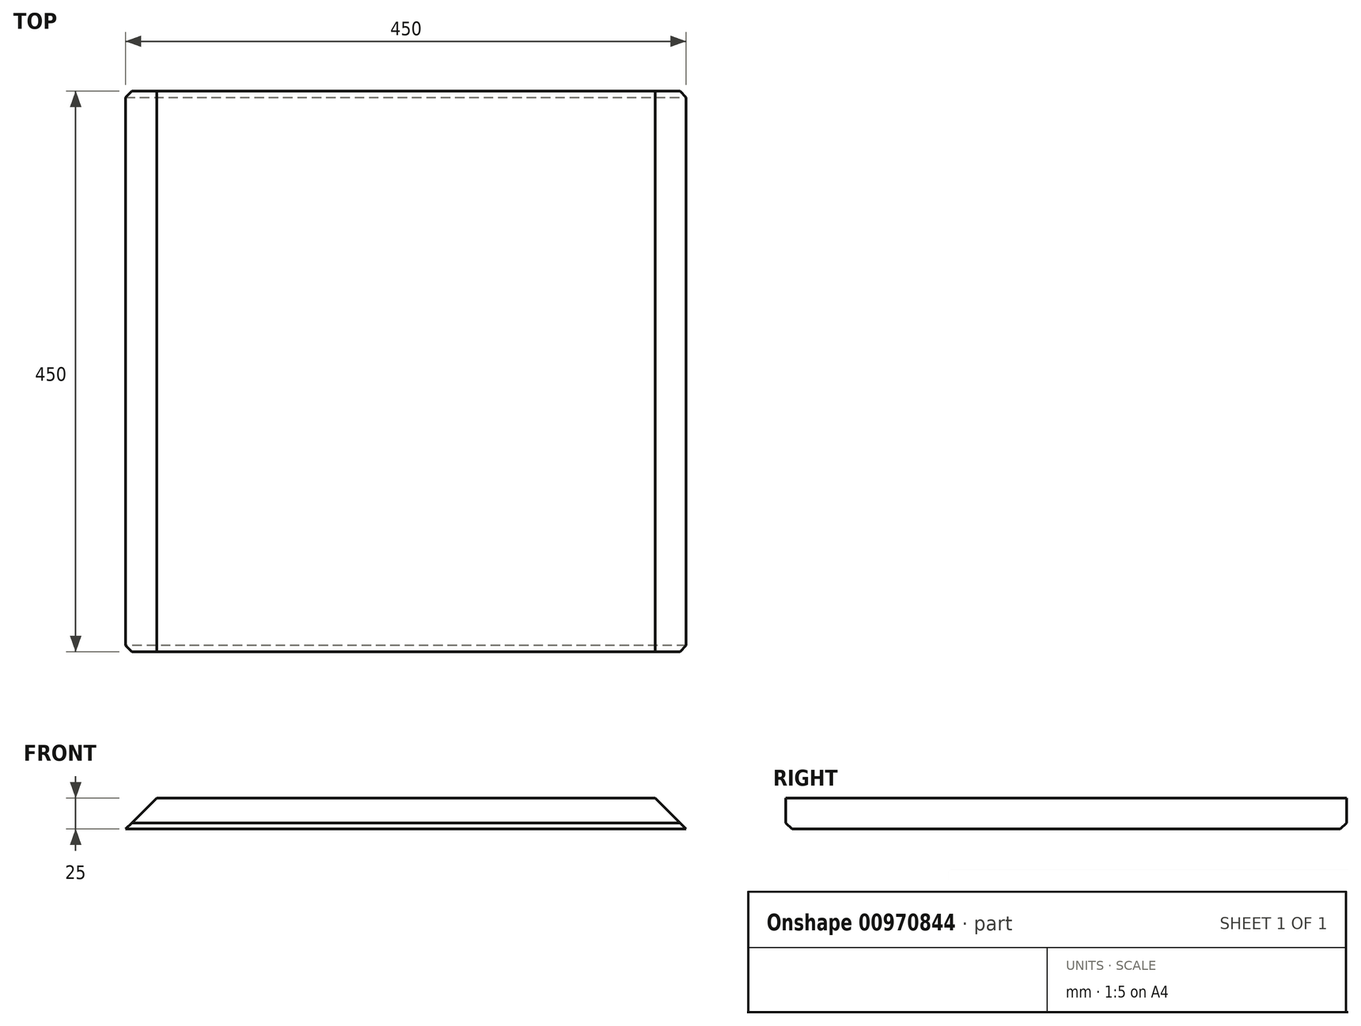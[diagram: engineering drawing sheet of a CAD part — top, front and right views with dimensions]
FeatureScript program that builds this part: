
annotation { "Feature Type Name" : "Feature", "Feature Type Description" : "" }
export const myFeature = defineFeature(function(context is Context, id is Id, definition is map)
    precondition{}
    {
        {
            var Q0;
            Q0=qCreatedBy(makeId("Front.planeOp"),FACE);
            var sketch = newSketch(context, id + "F0", { "sketchPlane" : qUnion([Q0])});
            skLineSegment(sketch, "E0.bottom", {"start": v(44.22, -7.61) * mm, "end": v(494.22, -7.61) * mm});
            skLineSegment(sketch, "E0.top", {"start": v(44.22, -32.61) * mm, "end": v(494.22, -32.61) * mm});
            skLineSegment(sketch, "E0.left", {"start": v(44.22, -7.61) * mm, "end": v(44.22, -32.61) * mm});
            skLineSegment(sketch, "E0.right", {"start": v(494.22, -7.61) * mm, "end": v(494.22, -32.61) * mm});
            skSolve(sketch);
        }
        {
            var Q0;
            Q0 = qSketchRegion(id + "F0", true);
            extrude(context, id + "F1", {"entities" : qUnion([Q0]), "depth" : 450 * mm, "offsetDistance" : 25 * mm});
        }
        {
            var Q0;
            Q0=makeQuery(id+"F1.opExtrude","SWEPT_EDGE",EDGE,{"disambiguationData":[OSD([sQuery(id+"F0.wireOp",EDGE,"E0.bottom"),sQuery(id+"F0.wireOp",EDGE,"E0.left")])]});
            chamfer(context, id + "F2", {"entities" : qUnion([Q0]), "width" : 25 * mm, "tangentPropagation" : true});
        }
        {
            var Q0;
            Q0=makeQuery(id+"F1.opExtrude","SWEPT_EDGE",EDGE,{"disambiguationData":[OSD([sQuery(id+"F0.wireOp",EDGE,"E0.bottom"),sQuery(id+"F0.wireOp",EDGE,"E0.right")])]});
            chamfer(context, id + "F3", {"entities" : qUnion([Q0]), "width" : 25 * mm, "tangentPropagation" : true});
        }
        {
            var Q0;
            Q0=makeQuery(id+"F1.opExtrude","CAP_EDGE",EDGE,{"disambiguationData":[OSD([sQuery(id+"F0.wireOp",EDGE,"E0.top")])],"isStart":false});
            var Q1;
            Q1=makeQuery(id+"F1.opExtrude","CAP_EDGE",EDGE,{"disambiguationData":[OSD([sQuery(id+"F0.wireOp",EDGE,"E0.top")])],"isStart":true});
            chamfer(context, id + "F4", {"entities" : qUnion([Q0, Q1]), "width" : 5 * mm, "tangentPropagation" : true});
        }
    });
